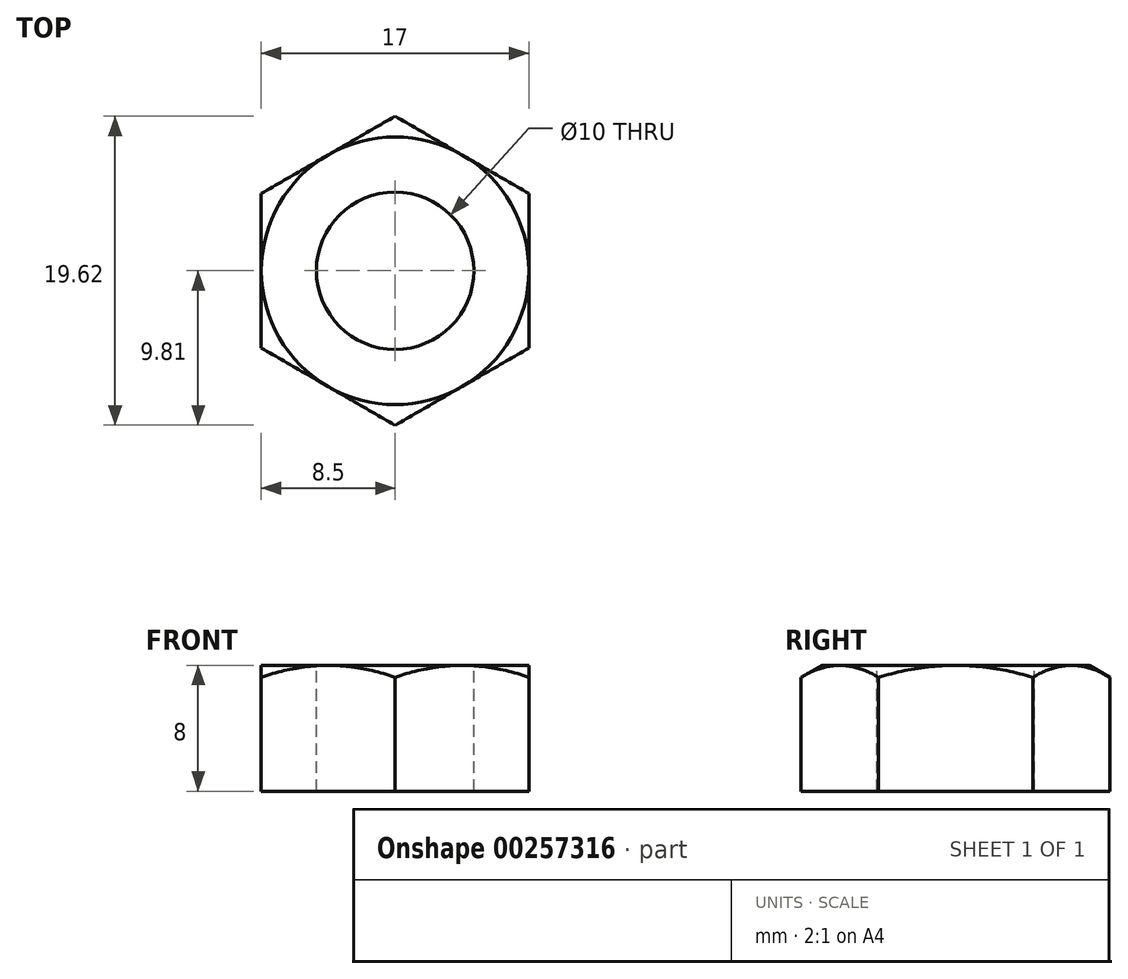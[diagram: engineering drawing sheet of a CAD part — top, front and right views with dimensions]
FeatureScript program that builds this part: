
annotation { "Feature Type Name" : "Feature", "Feature Type Description" : "" }
export const myFeature = defineFeature(function(context is Context, id is Id, definition is map)
    precondition{}
    {
        {
            var Q0;
            Q0=qCreatedBy(makeId("Top.planeOp"),FACE);
            var sketch = newSketch(context, id + "F0", { "sketchPlane" : qUnion([Q0])});
            skCircle(sketch, "E0.cCircle", {"center": v(0, 0) * mm, "radius": 8.5 * mm, "construction": true});
            skLineSegment(sketch, "E0.0", {"start": v(8.5, 4.9) * mm, "end": v(8.5, -4.9) * mm});
            skLineSegment(sketch, "E0.1", {"start": v(8.5, -4.9) * mm, "end": v(0, -9.81) * mm});
            skLineSegment(sketch, "E0.2", {"start": v(0, -9.81) * mm, "end": v(-8.5, -4.9) * mm});
            skLineSegment(sketch, "E0.3", {"start": v(-8.5, -4.9) * mm, "end": v(-8.5, 4.9) * mm});
            skLineSegment(sketch, "E0.4", {"start": v(-8.5, 4.9) * mm, "end": v(0, 9.81) * mm});
            skLineSegment(sketch, "E0.5", {"start": v(0, 9.81) * mm, "end": v(8.5, 4.9) * mm});
            skPoint(sketch, "E0.0.midPoint", {"position": v(8.5, 0) * mm});
            skSolve(sketch);
        }
        {
            var Q0;
            Q0=makeQuery(id+"F0.imprint","IMPRINT",FACE,{"disambiguationData":[TD([[makeQuery(id+"F0.imprint","IMPRINT",EDGE,{"derivedFrom":sQuery(id+"F0.wireOp",EDGE,"E0.0")}),-1.0]])]});
            extrude(context, id + "F1", {"entities" : qUnion([Q0]), "oppositeDirection" : true, "depth" : 8 * mm});
        }
        {
            var Q0;
            Q0=qCreatedBy(makeId("Right.planeOp"),FACE);
            var sketch = newSketch(context, id + "F2", { "sketchPlane" : qUnion([Q0])});
            skLineSegment(sketch, "E1", {"start": v(8.5, 0) * mm, "end": v(13.81, -3.07) * mm});
            skLineSegment(sketch, "E2", {"start": v(13.81, -3.07) * mm, "end": v(13.81, 0) * mm});
            skLineSegment(sketch, "E3", {"start": v(13.81, 0) * mm, "end": v(8.5, 0) * mm});
            skLineSegment(sketch, "E4", {"start": v(0, 6.93) * mm, "end": v(0, -13.88) * mm, "construction": true});
            skSolve(sketch);
        }
        {
            var Q0;
            Q0=makeQuery(id+"F2.imprint","IMPRINT",FACE,{"disambiguationData":[TD([[makeQuery(id+"F2.imprint","IMPRINT",EDGE,{"derivedFrom":sQuery(id+"F2.wireOp",EDGE,"E1")}),1.0]])]});
            var Q1;
            Q1=sQuery(id+"F2.wireOp",EDGE,"E4");
            revolve(context, id + "F3", {"operationType" : NewBodyOperationType.REMOVE, "entities" : qUnion([Q0]), "axis" : qUnion([Q1]), "revolveType" : RevolveType.FULL, "oppositeDirection" : true});
        }
        {
            var Q0;
            Q0=sQuery(id+"F0.wireOp",VERTEX,"E0.cCircle.center");
            var Q1;
            Q1=makeQuery(id+"F1.opExtrude","SWEPT_BODY",BODY,{"disambiguationData":[OSD([sQuery(id+"F0.wireOp",EDGE,"E0.0"),sQuery(id+"F0.wireOp",EDGE,"E0.1"),sQuery(id+"F0.wireOp",EDGE,"E0.2"),sQuery(id+"F0.wireOp",EDGE,"E0.3"),sQuery(id+"F0.wireOp",EDGE,"E0.4"),sQuery(id+"F0.wireOp",EDGE,"E0.5")])]});
            hole(context, id + "F4", {"style" : HoleStyle.SIMPLE, "endStyle" : HoleEndStyle.THROUGH, "holeDiameter" : 10 * mm, "tappedDepth" : 12 * mm, "tapClearance" : 3, "locations" : qUnion([Q0]), "scope" : qUnion([Q1])});
        }
    });
